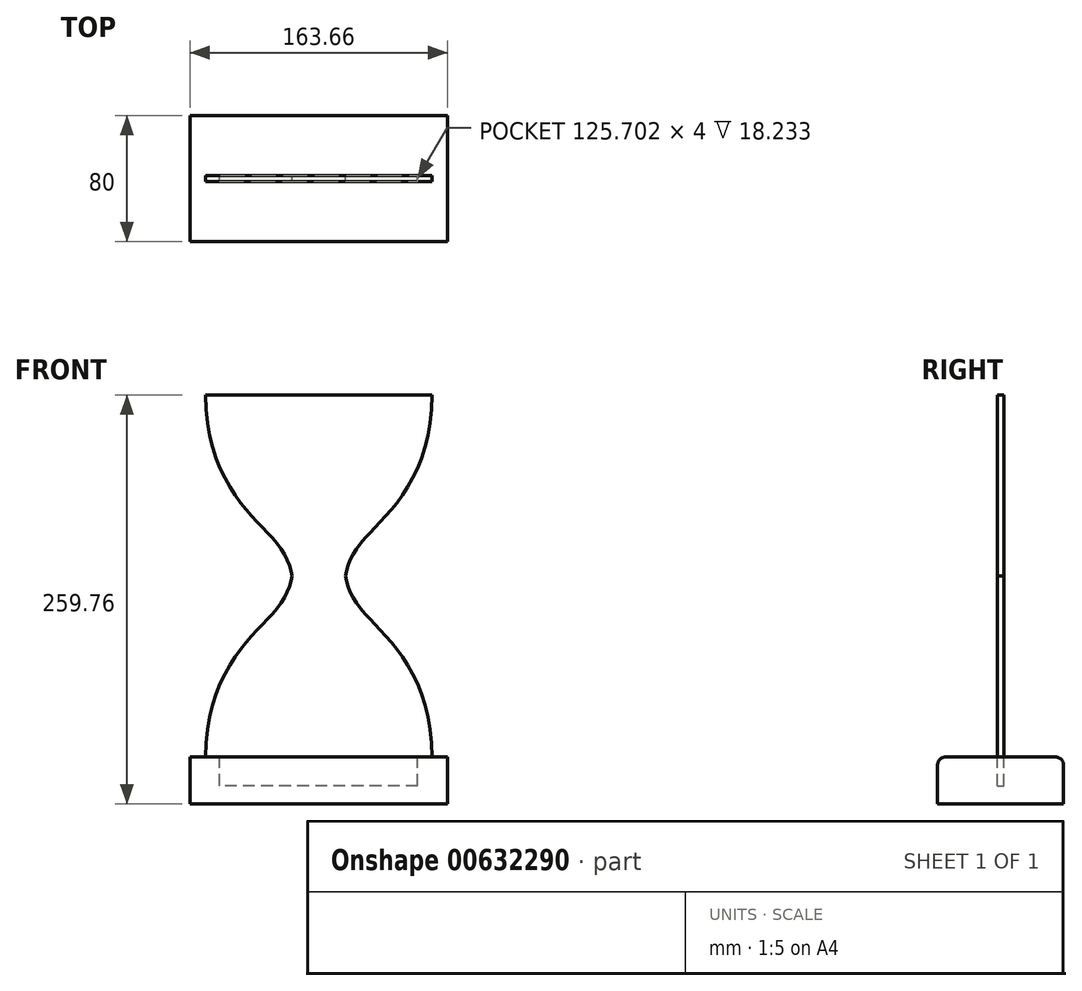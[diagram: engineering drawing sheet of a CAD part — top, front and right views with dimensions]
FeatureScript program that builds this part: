
annotation { "Feature Type Name" : "Feature", "Feature Type Description" : "" }
export const myFeature = defineFeature(function(context is Context, id is Id, definition is map)
    precondition{}
    {
        {
            var Q0;
            Q0=qCreatedBy(makeId("Front.planeOp"),FACE);
            var sketch = newSketch(context, id + "F0", { "sketchPlane" : qUnion([Q0])});
            skFitSpline(sketch, "E0", {"points": [v(-71.84, 115) * mm, v(-48.2, 44.74) * mm, v(-25.2, 18.9) * mm, v(-17.01, 0) * mm], "startDerivative": vector(-1.89, -215.2) * mm, "endDerivative": vector(6.48, -71.32) * mm});
            skFitSpline(sketch, "E1.MirrorCS", {"points": [v(71.84, 115) * mm, v(48.2, 44.74) * mm, v(25.2, 18.9) * mm, v(17.01, 0) * mm], "startDerivative": vector(1.89, -215.2) * mm, "endDerivative": vector(-6.48, -71.32) * mm});
            skFitSpline(sketch, "E2.MirrorCS", {"points": [v(-71.84, -115) * mm, v(-48.2, -44.74) * mm, v(-25.2, -18.9) * mm, v(-17.01, 0) * mm], "startDerivative": vector(-1.89, 215.2) * mm, "endDerivative": vector(6.48, 71.32) * mm});
            skFitSpline(sketch, "E3.MirrorCS", {"points": [v(71.84, -115) * mm, v(48.2, -44.74) * mm, v(25.2, -18.9) * mm, v(17.01, 0) * mm], "startDerivative": vector(1.89, 215.2) * mm, "endDerivative": vector(-6.48, 71.32) * mm});
            skLineSegment(sketch, "E4", {"start": v(-71.84, 115) * mm, "end": v(71.84, 115) * mm});
            skLineSegment(sketch, "E5", {"start": v(-71.84, -115) * mm, "end": v(71.84, -115) * mm});
            skLineSegment(sketch, "E6.bottom", {"start": v(62.85, -133.23) * mm, "end": v(-62.85, -133.23) * mm});
            skLineSegment(sketch, "E6.top", {"start": v(62.85, -115) * mm, "end": v(-62.85, -115) * mm});
            skLineSegment(sketch, "E6.left", {"start": v(62.85, -133.23) * mm, "end": v(62.85, -115) * mm});
            skLineSegment(sketch, "E6.right", {"start": v(-62.85, -133.23) * mm, "end": v(-62.85, -115) * mm});
            skPoint(sketch, "E6.middle", {"position": v(0, -124.12) * mm});
            skPoint(sketch, "E6.middle.positionSnap0", {"position": v(0, -115) * mm});
            skPoint(sketch, "E6.centerSnap0", {"position": v(0, -115) * mm});
            skSolve(sketch);
        }
        {
            var Q0;
            Q0 = qSketchRegion(id + "F0", true);
            extrude(context, id + "F1", {"entities" : qUnion([Q0]), "endBound" : BoundingType.SYMMETRIC, "depth" : 4 * mm, "offsetDistance" : 25 * mm});
        }
        {
            var Q0;
            Q0=makeQuery(id+"F1.opExtrude","CAP_FACE",FACE,{"disambiguationData":[OSD([sQuery(id+"F0.wireOp",EDGE,"E0"),sQuery(id+"F0.wireOp",EDGE,"E1.MirrorCS"),sQuery(id+"F0.wireOp",EDGE,"E2.MirrorCS"),sQuery(id+"F0.wireOp",EDGE,"E3.MirrorCS"),sQuery(id+"F0.wireOp",EDGE,"E4"),sQuery(id+"F0.wireOp",EDGE,"E5")])],"isStart":false});
            var sketch = newSketch(context, id + "F2", { "sketchPlane" : qUnion([Q0])});
            skFitSpline(sketch, "E7", {"points": [v(-20.24, 34.57) * mm, v(-7.59, 8) * mm, v(-1.43, -71.07) * mm], "startDerivative": vector(37.86, -59.37) * mm, "endDerivative": vector(2.6, -144.97) * mm});
            skFitSpline(sketch, "E8.MirrorCS", {"points": [v(20.24, 34.57) * mm, v(7.59, 8) * mm, v(1.43, -71.07) * mm], "startDerivative": vector(-37.86, -59.37) * mm, "endDerivative": vector(-2.6, -144.97) * mm});
            skArc(sketch, "E9", {"start": v(-1.43, -71.07) * mm, "mid": v(0, -72.67) * mm, "end": v(1.43, -71.07) * mm});
            skLineSegment(sketch, "E10", {"start": v(0, 87.33) * mm, "end": v(0, 78.93) * mm, "construction": true});
            skLineSegment(sketch, "E11.right", {"start": v(-25.5, 44.38) * mm, "end": v(-25.5, 53.44) * mm});
            skPoint(sketch, "E11.middle", {"position": v(0, 48.9) * mm});
            skArc(sketch, "E12", {"start": v(0, 78.93) * mm, "mid": v(-18.03, 71.46) * mm, "end": v(-25.5, 53.44) * mm});
            skArc(sketch, "E13", {"start": v(-25.5, 44.38) * mm, "mid": v(-15.84, 30.8) * mm, "end": v(0, 25.58) * mm});
            skLineSegment(sketch, "E14", {"start": v(0, 78.93) * mm, "end": v(0, 52.27) * mm, "construction": true});
            skLineSegment(sketch, "E15", {"start": v(0, 53.44) * mm, "end": v(-25.5, 53.44) * mm});
            skLineSegment(sketch, "E16", {"start": v(0, 44.38) * mm, "end": v(-25.5, 44.38) * mm});
            skPoint(sketch, "E11.left.end.orphan", {"position": v(25.5, 53.44) * mm});
            skPoint(sketch, "E17.end.orphan", {"position": v(25.5, 44.38) * mm});
            skLineSegment(sketch, "E18.trimOffspring", {"start": v(0, 44.38) * mm, "end": v(0, -91.15) * mm, "construction": true});
            skSolve(sketch);
        }
        {
            var Q0;
            Q0=qCreatedBy(makeId("Front.planeOp"),FACE);
            var sketch = newSketch(context, id + "F3", { "sketchPlane" : qUnion([Q0])});
            skLineSegment(sketch, "E19.bottom", {"start": v(81.83, -144.76) * mm, "end": v(-81.83, -144.76) * mm});
            skLineSegment(sketch, "E19.top", {"start": v(81.83, -115) * mm, "end": v(-81.83, -115) * mm});
            skLineSegment(sketch, "E19.left", {"start": v(81.83, -144.76) * mm, "end": v(81.83, -115) * mm});
            skLineSegment(sketch, "E19.right", {"start": v(-81.83, -144.76) * mm, "end": v(-81.83, -115) * mm});
            skPoint(sketch, "E19.middle", {"position": v(0, -129.88) * mm});
            skSolve(sketch);
        }
        {
            var Q0;
            Q0=makeQuery(id+"F3.imprint","IMPRINT",FACE,{"disambiguationData":[TD([[makeQuery(id+"F3.imprint","IMPRINT",EDGE,{"derivedFrom":sQuery(id+"F3.wireOp",EDGE,"E19.bottom")}),-1.0]])]});
            extrude(context, id + "F4", {"entities" : qUnion([Q0]), "endBound" : BoundingType.SYMMETRIC, "depth" : 80 * mm, "offsetDistance" : 25 * mm});
        }
        {
            var Q0;
            Q0=makeQuery(id+"F1.opExtrude","SWEPT_BODY",BODY,{"disambiguationData":[OSD([sQuery(id+"F0.wireOp",EDGE,"E0"),sQuery(id+"F0.wireOp",EDGE,"E1.MirrorCS"),sQuery(id+"F0.wireOp",EDGE,"E2.MirrorCS"),sQuery(id+"F0.wireOp",EDGE,"E3.MirrorCS"),sQuery(id+"F0.wireOp",EDGE,"E4"),sQuery(id+"F0.wireOp",EDGE,"E5"),sQuery(id+"F0.wireOp",EDGE,"E6.bottom"),sQuery(id+"F0.wireOp",EDGE,"E6.left"),sQuery(id+"F0.wireOp",EDGE,"E6.right")])]});
            var Q1;
            Q1=makeQuery(id+"F4.opExtrude","SWEPT_BODY",BODY,{"disambiguationData":[OSD([sQuery(id+"F3.wireOp",EDGE,"E19.bottom"),sQuery(id+"F3.wireOp",EDGE,"E19.top"),sQuery(id+"F3.wireOp",EDGE,"E19.left"),sQuery(id+"F3.wireOp",EDGE,"E19.right")])]});
            booleanBodies(context, id + "F5", {"operationType" : BooleanOperationType.SUBTRACTION, "tools" : qUnion([Q0]), "targets" : qUnion([Q1]), "keepTools" : true});
        }
        {
            var Q0;
            Q0=sQuery(id+"F2.wireOp",EDGE,"E10");
            var Q1;
            Q1=sQuery(id+"F2.wireOp",EDGE,"E7");
            var Q2;
            Q2=sQuery(id+"F2.wireOp",EDGE,"E10");
            revolve(context, id + "F6", {"bodyType" : ToolBodyType.SURFACE, "surfaceEntities" : qUnion([Q0, Q1]), "axis" : qUnion([Q2]), "revolveType" : RevolveType.ONE_DIRECTION, "oppositeDirection" : true, "angle" : 180 * degree});
        }
        {
            var Q0;
            Q0=sQuery(id+"F2.wireOp",EDGE,"E12");
            var Q1;
            Q1=sQuery(id+"F2.wireOp",EDGE,"E11.right");
            var Q2;
            Q2=sQuery(id+"F2.wireOp",EDGE,"E13");
            var Q3;
            Q3=sQuery(id+"F2.wireOp",EDGE,"E10");
            revolve(context, id + "F7", {"bodyType" : ToolBodyType.SURFACE, "surfaceEntities" : qUnion([Q0, Q1, Q2]), "axis" : qUnion([Q3]), "revolveType" : RevolveType.ONE_DIRECTION, "oppositeDirection" : true, "angle" : 180 * degree});
        }
        {
            var Q0;
            Q0=makeQuery(id+"F4.opExtrude","CAP_EDGE",EDGE,{"disambiguationData":[OSD([sQuery(id+"F3.wireOp",EDGE,"E19.top")])],"isStart":false});
            var Q1;
            Q1=makeQuery(id+"F4.opExtrude","CAP_EDGE",EDGE,{"disambiguationData":[OSD([sQuery(id+"F3.wireOp",EDGE,"E19.top")])],"isStart":true});
            fillet(context, id + "F8", {"entities" : qUnion([Q0, Q1]), "radius" : 5 * mm, "tangentPropagation" : true, "allowEdgeOverflow" : false});
        }
    });
